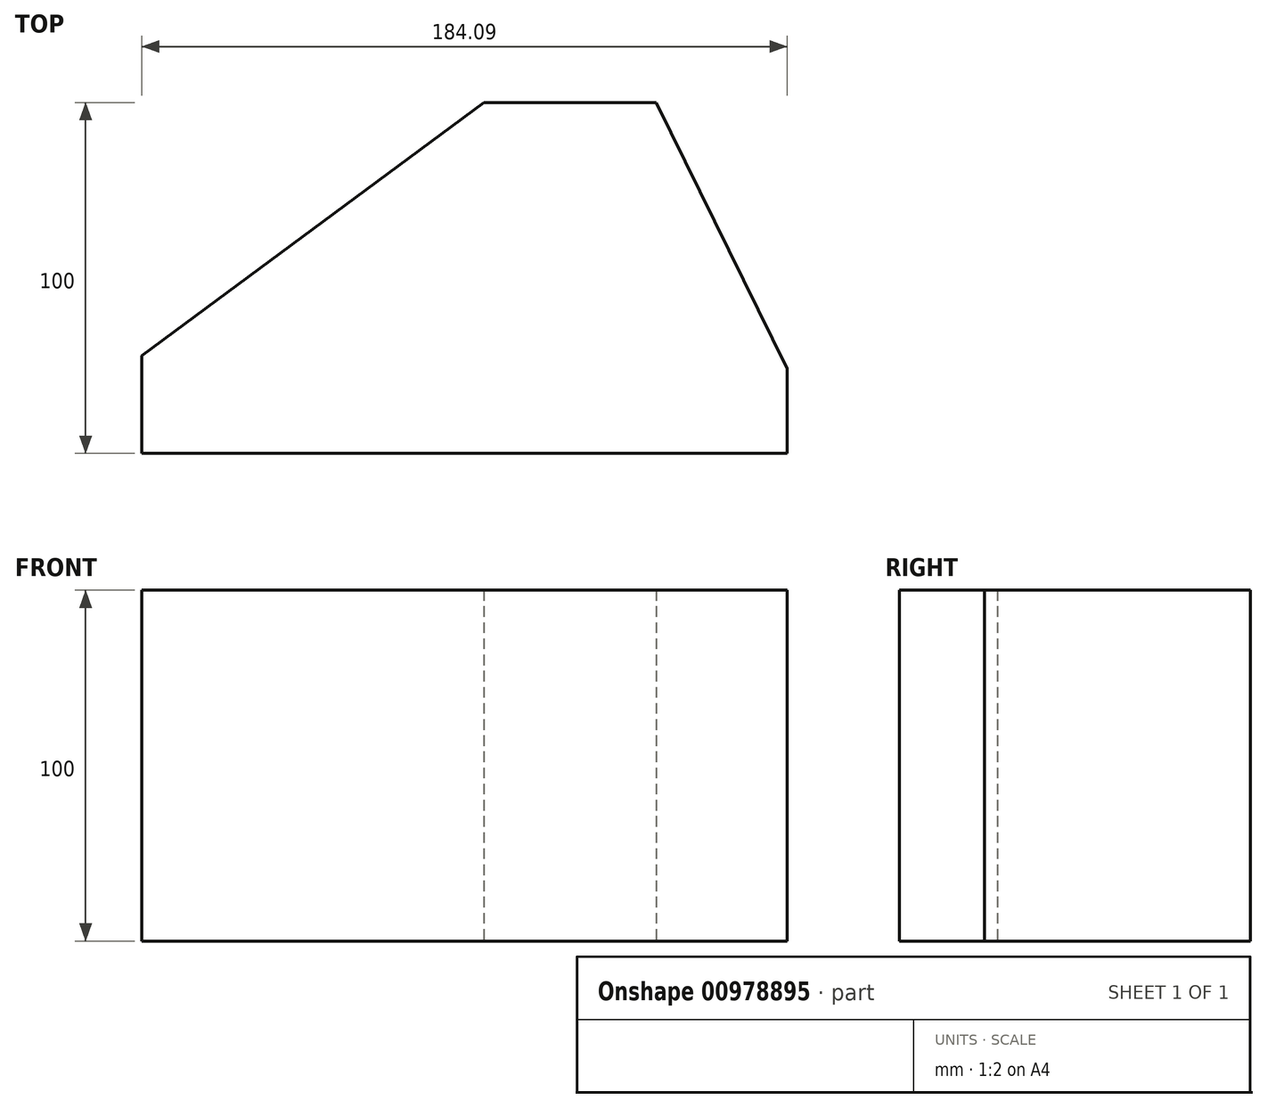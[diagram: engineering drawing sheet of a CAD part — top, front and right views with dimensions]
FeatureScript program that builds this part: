
annotation { "Feature Type Name" : "Feature", "Feature Type Description" : "" }
export const myFeature = defineFeature(function(context is Context, id is Id, definition is map)
    precondition{}
    {
        {
            var Q0;
            Q0=qCreatedBy(makeId("Top.planeOp"),FACE);
            var sketch = newSketch(context, id + "F0", { "sketchPlane" : qUnion([Q0])});
            skLineSegment(sketch, "E0", {"start": v(49.1, 0) * mm, "end": v(0, 0) * mm});
            skLineSegment(sketch, "E1", {"start": v(0, 0) * mm, "end": v(-97.56, -72.16) * mm});
            skLineSegment(sketch, "E2", {"start": v(-97.56, -72.16) * mm, "end": v(-97.56, -100) * mm});
            skLineSegment(sketch, "E3", {"start": v(-97.56, -100) * mm, "end": v(86.53, -100) * mm});
            skLineSegment(sketch, "E4", {"start": v(86.53, -100) * mm, "end": v(86.53, -75.82) * mm});
            skLineSegment(sketch, "E5", {"start": v(86.53, -75.82) * mm, "end": v(49.1, 0) * mm});
            skSolve(sketch);
        }
        {
            var Q0;
            Q0=makeQuery(id+"F0.imprint","IMPRINT",FACE,{"disambiguationData":[TD([[makeQuery(id+"F0.imprint","IMPRINT",EDGE,{"derivedFrom":sQuery(id+"F0.wireOp",EDGE,"E0")}),1.0]])]});
            extrude(context, id + "F1", {"entities" : qUnion([Q0]), "depth" : 100 * mm, "offsetDistance" : 25 * mm});
        }
    });
